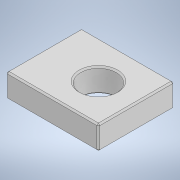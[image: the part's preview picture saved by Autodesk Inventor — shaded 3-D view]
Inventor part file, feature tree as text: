
AUTODESK INVENTOR PART (.ipt)
format: ipt  version: 2020.5 (Build 245400000, 400)  size: 123,904 bytes
history: native  units: mm
features: extrude x1, chamfer x1, sketch x1
ambient origin geometry x8: Origin, YZ Plane, XZ Plane, XY Plane, X Axis, Y Axis, Z Axis, Center Point
bodies: Solid1 (feature_tree)
feature tree (3):
  extrude  "Extrusion1"  Depth=4.0mm
  chamfer  "Chamfer1"  Distance=9.35mm
  sketch  "Sketch1"  dims[d0=15.85mm d1=13.0mm d2=9.35mm d3=6.5mm d4=6.0mm d9=4.0mm d10=0.0mm d11=0.25mm d12=2.0mm d13=45.0deg]
